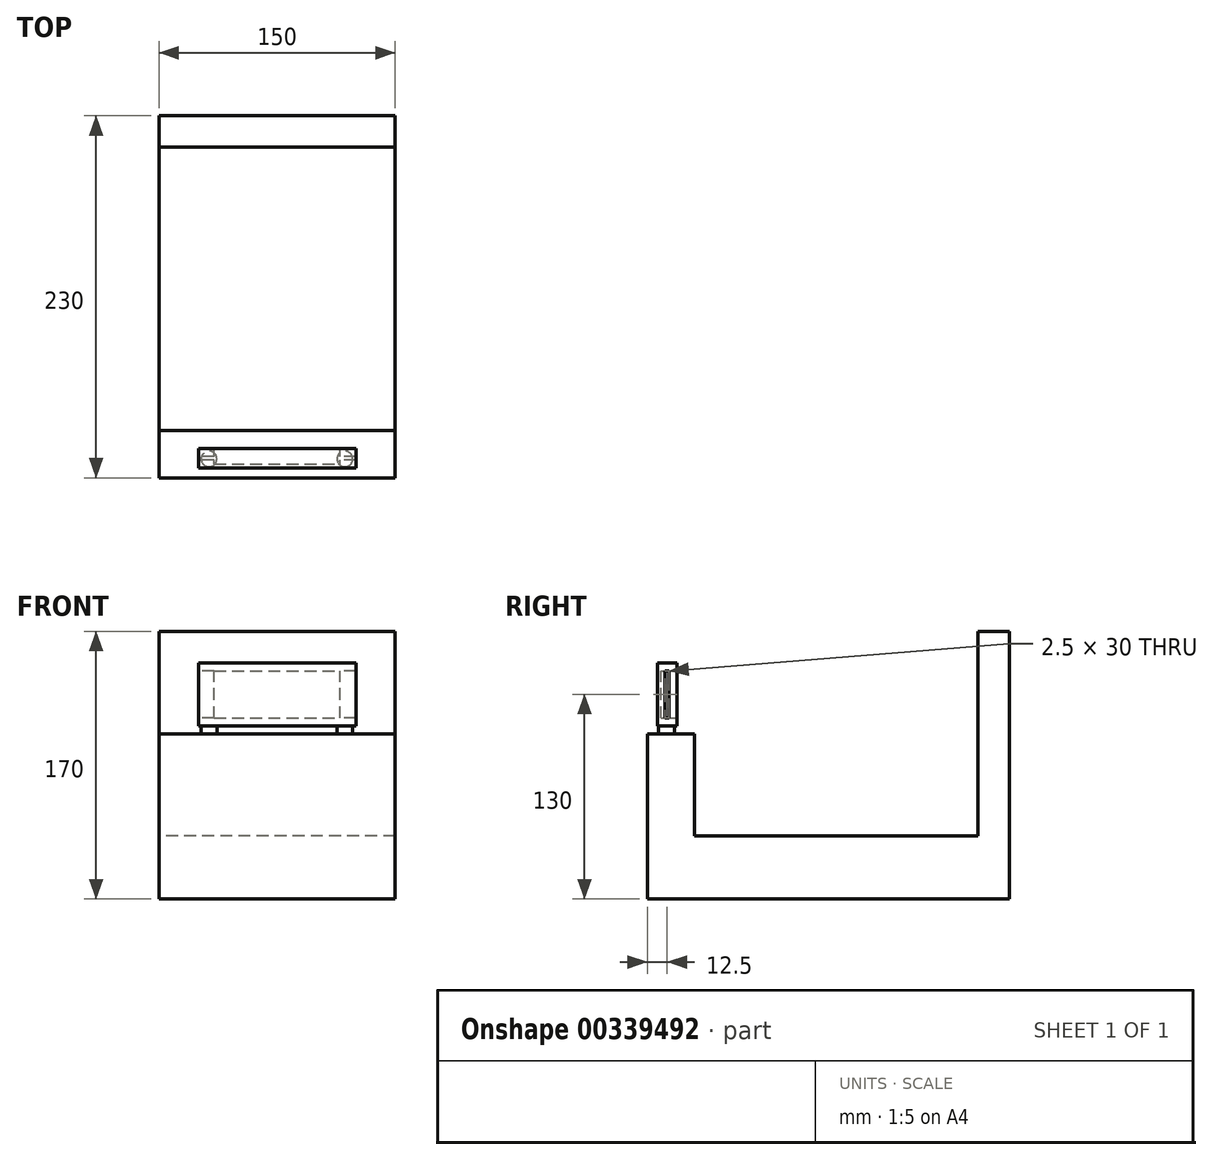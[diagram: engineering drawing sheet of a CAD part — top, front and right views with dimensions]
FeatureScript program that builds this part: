
annotation { "Feature Type Name" : "Feature", "Feature Type Description" : "" }
export const myFeature = defineFeature(function(context is Context, id is Id, definition is map)
    precondition{}
    {
        {
            var Q0;
            Q0=qCreatedBy(makeId("Right.planeOp"),FACE);
            var sketch = newSketch(context, id + "F0", { "sketchPlane" : qUnion([Q0])});
            skLineSegment(sketch, "E0.bottom", {"start": v(-115, -20) * mm, "end": v(115, -20) * mm});
            skLineSegment(sketch, "E0.top", {"start": v(-85, 20) * mm, "end": v(95, 20) * mm});
            skLineSegment(sketch, "E0.left", {"start": v(-115, -20) * mm, "end": v(-115, 20) * mm});
            skLineSegment(sketch, "E0.right", {"start": v(115, -20) * mm, "end": v(115, 20) * mm});
            skPoint(sketch, "E0.middle", {"position": v(0, 0) * mm});
            skLineSegment(sketch, "E1.top", {"start": v(115, 150) * mm, "end": v(95, 150) * mm});
            skLineSegment(sketch, "E1.left", {"start": v(115, 20) * mm, "end": v(115, 150) * mm});
            skLineSegment(sketch, "E1.right", {"start": v(95, 20) * mm, "end": v(95, 150) * mm});
            skLineSegment(sketch, "E2.top", {"start": v(-115, 85) * mm, "end": v(-85, 85) * mm});
            skLineSegment(sketch, "E2.left", {"start": v(-115, 20) * mm, "end": v(-115, 85) * mm});
            skLineSegment(sketch, "E2.right", {"start": v(-85, 20) * mm, "end": v(-85, 85) * mm});
            skSolve(sketch);
        }
        {
            var Q0;
            Q0 = qSketchRegion(id + "F0", true);
            extrude(context, id + "F1", {"entities" : qUnion([Q0]), "endBound" : BoundingType.SYMMETRIC, "depth" : 150 * mm});
        }
        {
            var Q0;
            Q0=qCreatedBy(makeId("Right.planeOp"),FACE);
            var sketch = newSketch(context, id + "F2", { "sketchPlane" : qUnion([Q0])});
            skLineSegment(sketch, "E3.bottom", {"start": v(-108.75, 130) * mm, "end": v(-96.25, 130) * mm});
            skLineSegment(sketch, "E3.top", {"start": v(-108.75, 90) * mm, "end": v(-96.25, 90) * mm});
            skLineSegment(sketch, "E3.left", {"start": v(-108.75, 130) * mm, "end": v(-108.75, 90) * mm});
            skLineSegment(sketch, "E3.right", {"start": v(-96.25, 130) * mm, "end": v(-96.25, 90) * mm});
            skLineSegment(sketch, "E4.bottom", {"start": v(-103.75, 125) * mm, "end": v(-101.25, 125) * mm});
            skLineSegment(sketch, "E4.top", {"start": v(-103.75, 95) * mm, "end": v(-101.25, 95) * mm});
            skLineSegment(sketch, "E4.left", {"start": v(-103.75, 125) * mm, "end": v(-103.75, 95) * mm});
            skLineSegment(sketch, "E4.right", {"start": v(-101.25, 125) * mm, "end": v(-101.25, 95) * mm});
            skSolve(sketch);
        }
        {
            var Q0;
            Q0 = qSketchRegion(id + "F2", true);
            extrude(context, id + "F3", {"entities" : qUnion([Q0]), "endBound" : BoundingType.SYMMETRIC, "depth" : 100 * mm});
        }
        {
            var Q0;
            Q0=makeQuery(id+"F3.opExtrude","SWEPT_FACE",FACE,{"disambiguationData":[OSD([sQuery(id+"F2.wireOp",EDGE,"E3.right")])]});
            var sketch = newSketch(context, id + "F4", { "sketchPlane" : qUnion([Q0])});
            skLineSegment(sketch, "E5.bottom", {"start": v(40, 95) * mm, "end": v(-40, 95) * mm});
            skLineSegment(sketch, "E5.top", {"start": v(40, 125) * mm, "end": v(-40, 125) * mm});
            skLineSegment(sketch, "E5.left", {"start": v(40, 95) * mm, "end": v(40, 125) * mm});
            skLineSegment(sketch, "E5.right", {"start": v(-40, 95) * mm, "end": v(-40, 125) * mm});
            skPoint(sketch, "E5.middle", {"position": v(0, 110) * mm});
            skPoint(sketch, "E5.middle.positionSnap0", {"position": v(-50, 110) * mm});
            skPoint(sketch, "E5.centerSnap0", {"position": v(-50, 110) * mm});
            skSolve(sketch);
        }
        {
            var Q0;
            Q0=makeQuery(id+"F4.imprint","IMPRINT",FACE,{"disambiguationData":[TD([[makeQuery(id+"F4.imprint","IMPRINT",EDGE,{"derivedFrom":sQuery(id+"F4.wireOp",EDGE,"E5.bottom")}),-1.0]])]});
            extrude(context, id + "F5", {"entities" : qUnion([Q0]), "operationType" : NewBodyOperationType.REMOVE, "oppositeDirection" : true, "depth" : 10 * mm});
        }
        {
            var Q0;
            Q0=makeQuery(id+"F3.opExtrude","SWEPT_FACE",FACE,{"disambiguationData":[OSD([sQuery(id+"F2.wireOp",EDGE,"E3.top")])]});
            var sketch = newSketch(context, id + "F6", { "sketchPlane" : qUnion([Q0])});
            skCircle(sketch, "E6", {"center": v(43.05, 102.92) * mm, "radius": 5 * mm});
            skCircle(sketch, "E7", {"center": v(-43.24, 102.92) * mm, "radius": 5 * mm});
            skSolve(sketch);
        }
        {
            var Q0;
            Q0 = qSketchRegion(id + "F6", true);
            var Q1;
            Q1=makeQuery(id+"F1.opExtrude","SWEPT_FACE",FACE,{"disambiguationData":[OSD([sQuery(id+"F0.wireOp",EDGE,"E2.top")])]});
            extrude(context, id + "F7", {"entities" : qUnion([Q0]), "endBound" : BoundingType.UP_TO_SURFACE, "endBoundEntityFace" : qUnion([Q1]), "depth" : 25 * mm});
        }
    });
